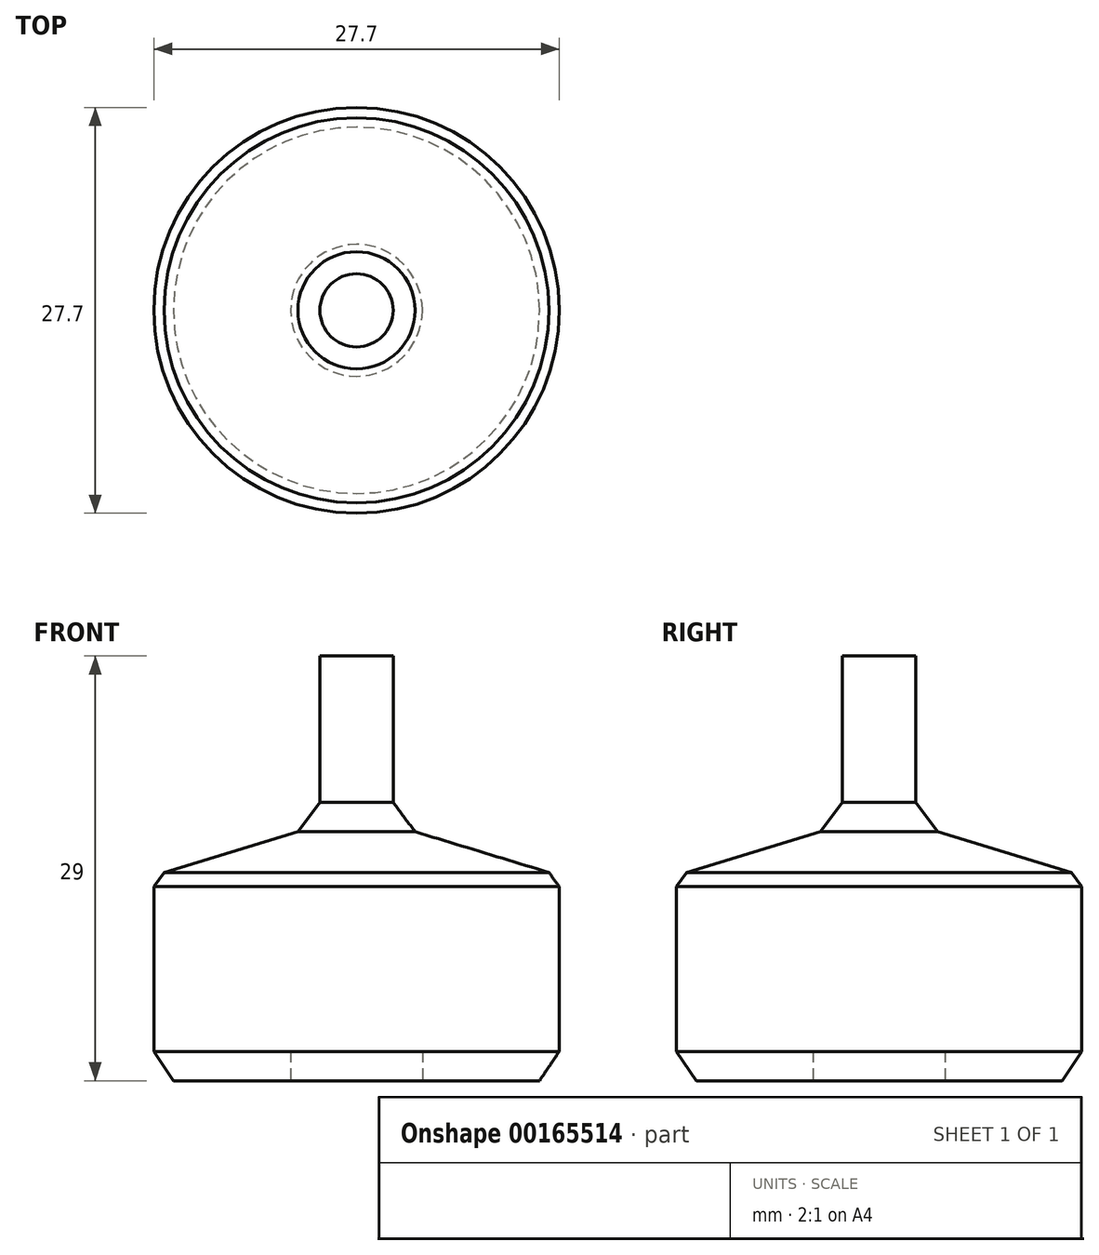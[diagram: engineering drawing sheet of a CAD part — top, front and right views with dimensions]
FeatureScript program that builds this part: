
annotation { "Feature Type Name" : "Feature", "Feature Type Description" : "" }
export const myFeature = defineFeature(function(context is Context, id is Id, definition is map)
    precondition{}
    {
        {
            var Q0;
            Q0=qCreatedBy(makeId("Top.planeOp"),FACE);
            cPlane(context, id + "F0", {"entities" : qUnion([Q0]), "cplaneType" : CPlaneType.OFFSET, "offset" : 2 * mm, "width" : 152.4 * mm, "height" : 152.4 * mm});
        }
        {
            var Q0;
            Q0=qCreatedBy(id+"F0.planeOp",FACE);
            cPlane(context, id + "F1", {"entities" : qUnion([Q0]), "cplaneType" : CPlaneType.OFFSET, "offset" : 12 * mm, "width" : 150 * mm, "height" : 150 * mm});
        }
        {
            var Q0;
            Q0=qCreatedBy(id+"F1.planeOp",FACE);
            cPlane(context, id + "F2", {"entities" : qUnion([Q0]), "cplaneType" : CPlaneType.OFFSET, "offset" : 3 * mm, "width" : 150 * mm, "height" : 150 * mm});
        }
        {
            var Q0;
            Q0=qCreatedBy(id+"F2.planeOp",FACE);
            cPlane(context, id + "F3", {"entities" : qUnion([Q0]), "cplaneType" : CPlaneType.OFFSET, "offset" : 2 * mm, "width" : 150 * mm, "height" : 150 * mm});
        }
        {
            var Q0;
            Q0=qCreatedBy(id+"F3.planeOp",FACE);
            cPlane(context, id + "F4", {"entities" : qUnion([Q0]), "cplaneType" : CPlaneType.OFFSET, "offset" : 10 * mm, "width" : 150 * mm, "height" : 150 * mm});
        }
        {
            var Q0;
            Q0=qCreatedBy(makeId("Top.planeOp"),FACE);
            var sketch = newSketch(context, id + "F5", { "sketchPlane" : qUnion([Q0])});
            skCircle(sketch, "E0", {"center": v(0, 0) * mm, "radius": 12.5 * mm});
            skSolve(sketch);
        }
        {
            var Q0;
            Q0=qCreatedBy(id+"F0.planeOp",FACE);
            var sketch = newSketch(context, id + "F6", { "sketchPlane" : qUnion([Q0])});
            skCircle(sketch, "E1", {"center": v(0, 0) * mm, "radius": 13.85 * mm});
            skSolve(sketch);
        }
        {
            var Q0;
            Q0=qCreatedBy(id+"F1.planeOp",FACE);
            var sketch = newSketch(context, id + "F7", { "sketchPlane" : qUnion([Q0])});
            skCircle(sketch, "E2", {"center": v(0, 0) * mm, "radius": 13.85 * mm});
            skSolve(sketch);
        }
        {
            var Q0;
            Q0=qCreatedBy(id+"F3.planeOp",FACE);
            var sketch = newSketch(context, id + "F8", { "sketchPlane" : qUnion([Q0])});
            skCircle(sketch, "E3", {"center": v(0, 0) * mm, "radius": 2.5 * mm});
            skSolve(sketch);
        }
        {
            var Q0;
            Q0=qCreatedBy(id+"F2.planeOp",FACE);
            var sketch = newSketch(context, id + "F9", { "sketchPlane" : qUnion([Q0])});
            skCircle(sketch, "E4", {"center": v(0, 0) * mm, "radius": 4 * mm});
            skSolve(sketch);
        }
        {
            var Q0;
            Q0=qCreatedBy(id+"F4.planeOp",FACE);
            var sketch = newSketch(context, id + "F10", { "sketchPlane" : qUnion([Q0])});
            skCircle(sketch, "E5", {"center": v(0, 0) * mm, "radius": 2.5 * mm});
            skSolve(sketch);
        }
        {
            var Q0;
            Q0=makeQuery(id+"F5.imprint","IMPRINT",FACE,{"disambiguationData":[TD([[makeQuery(id+"F5.imprint","IMPRINT",EDGE,{"derivedFrom":sQuery(id+"F5.wireOp",EDGE,"E0")}),1.0]])]});
            var Q1;
            Q1=makeQuery(id+"F6.imprint","IMPRINT",FACE,{"disambiguationData":[TD([[makeQuery(id+"F6.imprint","IMPRINT",EDGE,{"derivedFrom":sQuery(id+"F6.wireOp",EDGE,"E1")}),1.0]])]});
            loft(context, id + "F11", {"sheetProfilesArray" : [{ "sheetProfileEntities" : qUnion([Q0]) }, { "sheetProfileEntities" : qUnion([Q1]) }]});
        }
        {
            var Q1;
            Q1=makeQuery(id+"F11.opLoft","CAP_FACE",FACE,{"disambiguationData":[OSD([makeQuery(id+"F6.imprint","IMPRINT",FACE,{"disambiguationData":[TD([[makeQuery(id+"F6.imprint","IMPRINT",EDGE,{"derivedFrom":sQuery(id+"F6.wireOp",EDGE,"E1")}),1.0]])]})])],"isStart":true});
            var Q2;
            Q2=makeQuery(id+"F7.imprint","IMPRINT",FACE,{"disambiguationData":[TD([[makeQuery(id+"F7.imprint","IMPRINT",EDGE,{"derivedFrom":sQuery(id+"F7.wireOp",EDGE,"E2")}),1.0]])]});
            loft(context, id + "F12", {"operationType" : NewBodyOperationType.ADD, "sheetProfilesArray" : [{ "sheetProfileEntities" : qUnion([Q1]) }, { "sheetProfileEntities" : qUnion([Q2]) }]});
        }
        {
            var Q1;
            Q1=makeQuery(id+"F12.opLoft","CAP_FACE",FACE,{"disambiguationData":[OSD([makeQuery(id+"F7.imprint","IMPRINT",FACE,{"disambiguationData":[TD([[makeQuery(id+"F7.imprint","IMPRINT",EDGE,{"derivedFrom":sQuery(id+"F7.wireOp",EDGE,"E2")}),1.0]])]})])],"isStart":true});
            var Q2;
            Q2=makeQuery(id+"F9.imprint","IMPRINT",FACE,{"disambiguationData":[TD([[makeQuery(id+"F9.imprint","IMPRINT",EDGE,{"derivedFrom":sQuery(id+"F9.wireOp",EDGE,"E4")}),1.0]])]});
            loft(context, id + "F13", {"operationType" : NewBodyOperationType.ADD, "sheetProfilesArray" : [{ "sheetProfileEntities" : qUnion([Q1]) }, { "sheetProfileEntities" : qUnion([Q2]) }]});
        }
        {
            var Q1;
            Q1=makeQuery(id+"F13.opLoft","CAP_FACE",FACE,{"disambiguationData":[OSD([makeQuery(id+"F9.imprint","IMPRINT",FACE,{"disambiguationData":[TD([[makeQuery(id+"F9.imprint","IMPRINT",EDGE,{"derivedFrom":sQuery(id+"F9.wireOp",EDGE,"E4")}),1.0]])]})])],"isStart":true});
            var Q2;
            Q2=makeQuery(id+"F8.imprint","IMPRINT",FACE,{"disambiguationData":[TD([[makeQuery(id+"F8.imprint","IMPRINT",EDGE,{"derivedFrom":sQuery(id+"F8.wireOp",EDGE,"E3")}),1.0]])]});
            loft(context, id + "F14", {"operationType" : NewBodyOperationType.ADD, "sheetProfilesArray" : [{ "sheetProfileEntities" : qUnion([Q1]) }, { "sheetProfileEntities" : qUnion([Q2]) }]});
        }
        {
            var Q1;
            Q1=makeQuery(id+"F14.opLoft","CAP_FACE",FACE,{"disambiguationData":[OSD([makeQuery(id+"F8.imprint","IMPRINT",FACE,{"disambiguationData":[TD([[makeQuery(id+"F8.imprint","IMPRINT",EDGE,{"derivedFrom":sQuery(id+"F8.wireOp",EDGE,"E3")}),1.0]])]})])],"isStart":true});
            var Q2;
            Q2=makeQuery(id+"F10.imprint","IMPRINT",FACE,{"disambiguationData":[TD([[makeQuery(id+"F10.imprint","IMPRINT",EDGE,{"derivedFrom":sQuery(id+"F10.wireOp",EDGE,"E5")}),1.0]])]});
            loft(context, id + "F15", {"operationType" : NewBodyOperationType.ADD, "sheetProfilesArray" : [{ "sheetProfileEntities" : qUnion([Q1]) }, { "sheetProfileEntities" : qUnion([Q2]) }]});
        }
        {
            var Q0;
            {var subQ0=sQuery(id+"F7.wireOp",EDGE,"E2");var subQ1=sQuery(id+"F6.wireOp",EDGE,"E1");var subQ2=sQuery(id+"F5.wireOp",EDGE,"E0");Q0=makeQuery(id+"F13.boolean.opBoolean","MERGE",EDGE,{"derivedFrom":[makeQuery(id+"F12.opLoft","MID_CAP_EDGE",EDGE,{"disambiguationData":[OSD([subQ2,subQ1,subQ0])],"capPos":1.0}),makeQuery(id+"F13.opLoft","MID_CAP_EDGE",EDGE,{"disambiguationData":[OSD([subQ2,subQ1,subQ0])],"capPos":0.0})]});}
            chamfer(context, id + "F16", {"entities" : qUnion([Q0]), "width" : 1 * mm, "tangentPropagation" : true});
        }
        {
            var Q0;
            Q0=qCreatedBy(makeId("Top.planeOp"),FACE);
            var sketch = newSketch(context, id + "F17", { "sketchPlane" : qUnion([Q0])});
            skCircle(sketch, "E6", {"center": v(0, 0) * mm, "radius": 4.5 * mm});
            skSolve(sketch);
        }
        {
            var Q0;
            Q0=makeQuery(id+"F17.imprint","IMPRINT",FACE,{"disambiguationData":[TD([[makeQuery(id+"F17.imprint","IMPRINT",EDGE,{"derivedFrom":sQuery(id+"F17.wireOp",EDGE,"E6")}),1.0]])]});
            extrude(context, id + "F18", {"entities" : qUnion([Q0]), "operationType" : NewBodyOperationType.REMOVE, "depth" : 2 * mm});
        }
    });
